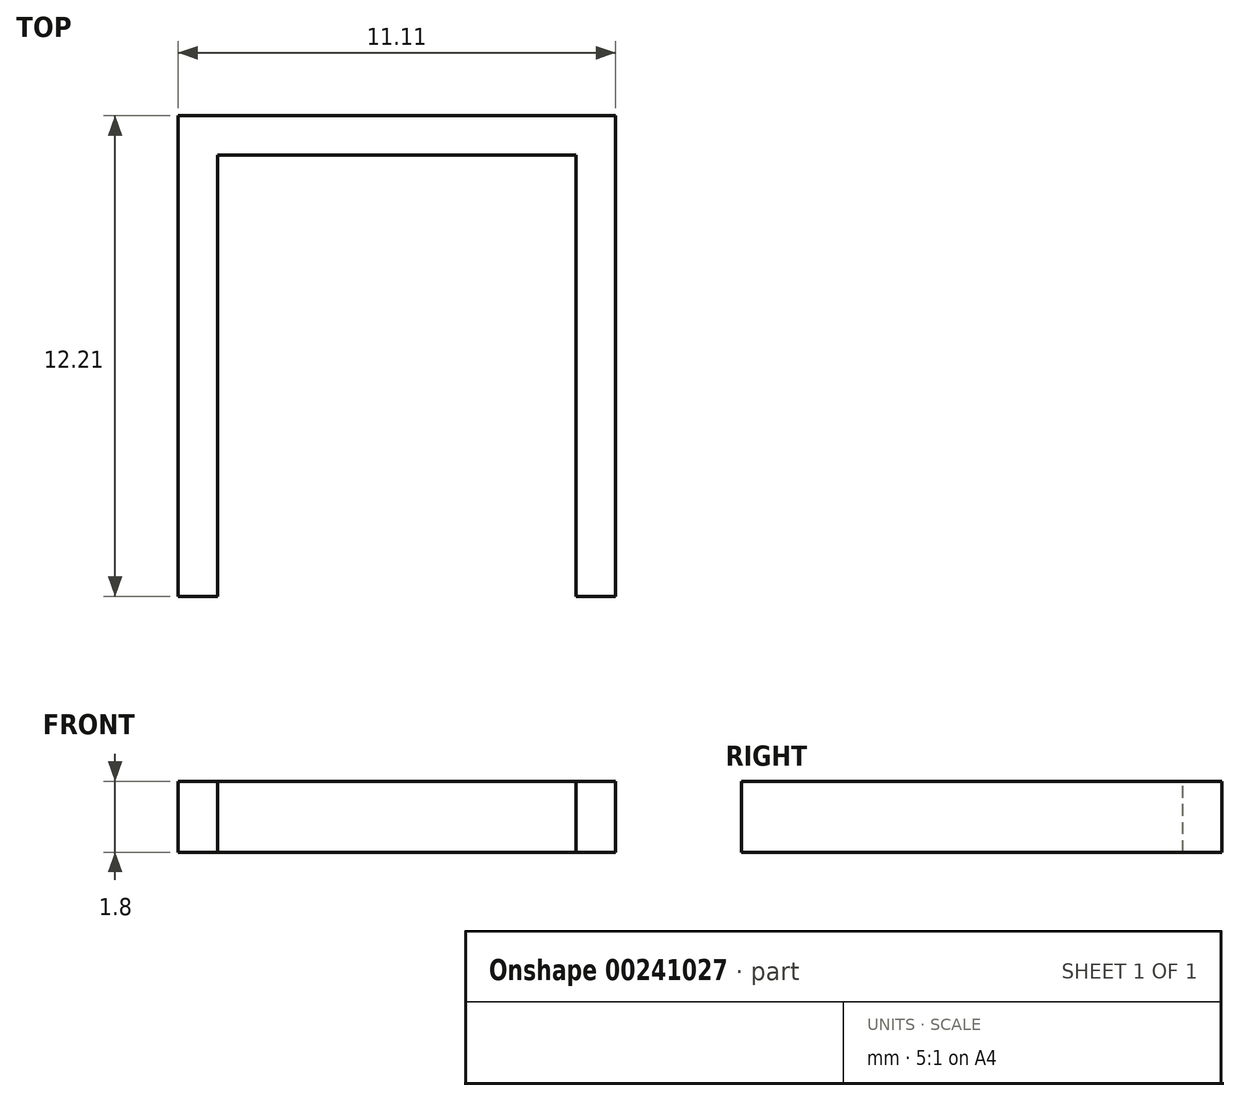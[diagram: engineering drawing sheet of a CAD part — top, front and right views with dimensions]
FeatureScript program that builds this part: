
annotation { "Feature Type Name" : "Feature", "Feature Type Description" : "" }
export const myFeature = defineFeature(function(context is Context, id is Id, definition is map)
    precondition{}
    {
        {
            var Q0;
            Q0=qCreatedBy(makeId("Top.planeOp"),FACE);
            var sketch = newSketch(context, id + "F0", { "sketchPlane" : qUnion([Q0])});
            skLineSegment(sketch, "E0.bottom", {"start": v(0, 0) * mm, "end": v(11.1, 0) * mm});
            skLineSegment(sketch, "E0.top", {"start": v(0, -12.21) * mm, "end": v(11.11, -12.21) * mm});
            skLineSegment(sketch, "E0.left", {"start": v(0, 0) * mm, "end": v(0, -12.21) * mm});
            skLineSegment(sketch, "E0.right", {"start": v(11.1, 0) * mm, "end": v(11.1, -12.2) * mm});
            skLineSegment(sketch, "E1.bottom", {"start": v(1, -12.21) * mm, "end": v(10.11, -12.21) * mm});
            skLineSegment(sketch, "E1.top", {"start": v(1, -1) * mm, "end": v(10.11, -1) * mm});
            skLineSegment(sketch, "E1.left", {"start": v(1, -12.21) * mm, "end": v(1, -1) * mm});
            skLineSegment(sketch, "E1.right", {"start": v(10.11, -12.21) * mm, "end": v(10.11, -1) * mm});
            skPoint(sketch, "E2", {"position": v(5.55, -1) * mm});
            skPoint(sketch, "E3", {"position": v(5.55, 0) * mm});
            skSolve(sketch);
        }
        {
            var Q0;
            Q0=makeQuery(id+"F0.imprint","IMPRINT",FACE,{"disambiguationData":[TD([[makeQuery(id+"F0.imprint","IMPRINT",EDGE,{"derivedFrom":sQuery(id+"F0.wireOp",EDGE,"E0.bottom")}),-1.0]])]});
            var Q1;
            Q1=makeQuery(id+"F0.imprint","IMPRINT",FACE,{"disambiguationData":[TD([[makeQuery(id+"F0.imprint","IMPRINT",EDGE,{"derivedFrom":sQuery(id+"F0.wireOp",EDGE,"E1.bottom")}),1.0]])]});
            extrude(context, id + "F1", {"entities" : qUnion([Q0, Q1]), "oppositeDirection" : true, "depth" : 0.6 * mm});
        }
        {
            var Q0;
            Q0=makeQuery(id+"F0.imprint","IMPRINT",FACE,{"disambiguationData":[TD([[makeQuery(id+"F0.imprint","IMPRINT",EDGE,{"derivedFrom":sQuery(id+"F0.wireOp",EDGE,"E0.bottom")}),-1.0]])]});
            extrude(context, id + "F2", {"entities" : qUnion([Q0]), "operationType" : NewBodyOperationType.ADD, "depth" : 1.2 * mm});
        }
    });
